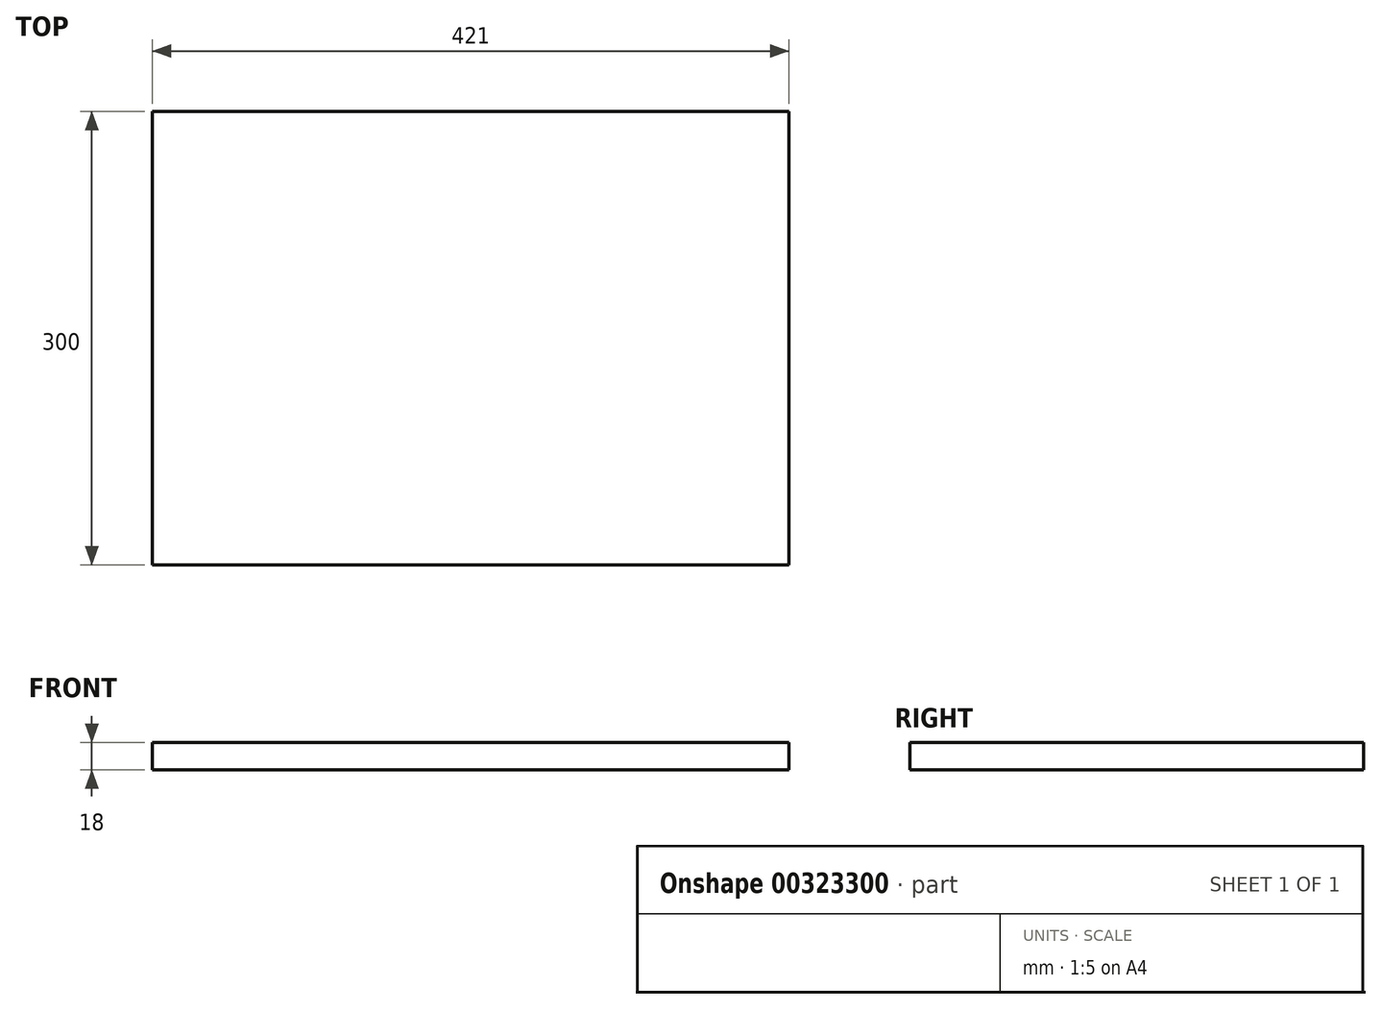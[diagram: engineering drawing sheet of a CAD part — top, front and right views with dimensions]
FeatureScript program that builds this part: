
annotation { "Feature Type Name" : "Feature", "Feature Type Description" : "" }
export const myFeature = defineFeature(function(context is Context, id is Id, definition is map)
    precondition{}
    {
        {
            var Q0;
            Q0=qCreatedBy(makeId("Top.planeOp"),FACE);
            var sketch = newSketch(context, id + "F0", { "sketchPlane" : qUnion([Q0])});
            skLineSegment(sketch, "E0.bottom", {"start": v(0, 6.97) * mm, "end": v(421, 6.97) * mm});
            skLineSegment(sketch, "E0.top", {"start": v(0, 306.97) * mm, "end": v(421, 306.97) * mm});
            skLineSegment(sketch, "E0.left", {"start": v(0, 6.97) * mm, "end": v(0, 306.97) * mm});
            skLineSegment(sketch, "E0.right", {"start": v(421, 6.97) * mm, "end": v(421, 306.97) * mm});
            skSolve(sketch);
        }
        {
            var Q0;
            Q0 = qSketchRegion(id + "F0", true);
            extrude(context, id + "F1", {"entities" : qUnion([Q0]), "depth" : 18 * mm, "offsetDistance" : 25 * mm});
        }
    });
